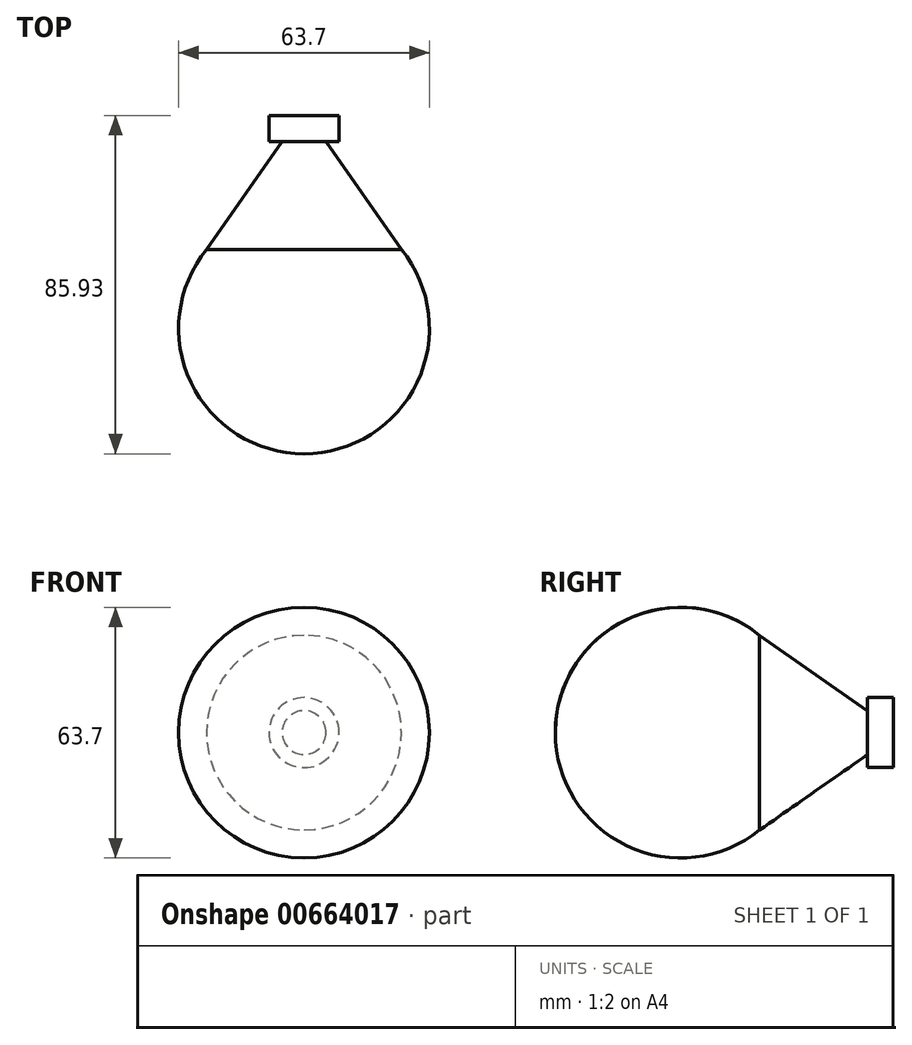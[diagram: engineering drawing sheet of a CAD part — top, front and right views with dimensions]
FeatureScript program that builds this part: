
annotation { "Feature Type Name" : "Feature", "Feature Type Description" : "" }
export const myFeature = defineFeature(function(context is Context, id is Id, definition is map)
    precondition{}
    {
        {
            var Q0;
            Q0=qCreatedBy(makeId("Front.planeOp"),FACE);
            var sketch = newSketch(context, id + "F0", { "sketchPlane" : qUnion([Q0])});
            skCircle(sketch, "E0", {"center": v(0, 0) * mm, "radius": 8.9 * mm});
            skSolve(sketch);
        }
        {
            var Q0;
            Q0=makeQuery(id+"F0.imprint","IMPRINT",FACE,{"disambiguationData":[TD([[makeQuery(id+"F0.imprint","IMPRINT",EDGE,{"derivedFrom":sQuery(id+"F0.wireOp",EDGE,"E0")}),1.0]])]});
            extrude(context, id + "F1", {"entities" : qUnion([Q0]), "oppositeDirection" : true, "depth" : 6.6 * mm, "offsetDistance" : 25.4 * mm});
        }
        {
            var Q0;
            Q0=qCreatedBy(makeId("Right.planeOp"),FACE);
            var sketch = newSketch(context, id + "F2", { "sketchPlane" : qUnion([Q0])});
            skCircle(sketch, "E1", {"center": v(-47.48, 0) * mm, "radius": 31.85 * mm});
            skPoint(sketch, "E2", {"position": v(0, 5.57) * mm});
            skLineSegment(sketch, "E3", {"start": v(-91.62, 0) * mm, "end": v(47.93, 0) * mm});
            skPoint(sketch, "E4.MirrorP", {"position": v(0, -5.57) * mm});
            skLineSegment(sketch, "E5", {"start": v(0, 5.57) * mm, "end": v(-27.42, 24.74) * mm});
            skLineSegment(sketch, "E6.MirrorCS", {"start": v(0, -5.57) * mm, "end": v(-27.42, -24.74) * mm});
            skLineSegment(sketch, "E7", {"start": v(0, 5.57) * mm, "end": v(0, -5.57) * mm});
            skSolve(sketch);
        }
        {
            var Q0;
            {var subQ0=sQuery(id+"F2.wireOp",EDGE,"E1");var subQ1=makeQuery(id+"F2.imprint","INTERSECT",VERTEX,{"derivedFrom":[subQ0,sQuery(id+"F2.wireOp",EDGE,"E5")]});Q0=makeQuery(id+"F2.imprint","IMPRINT",FACE,{"disambiguationData":[TD([[makeQuery(id+"F2.imprint","IMPRINT",EDGE,{"disambiguationData":[TD([[subQ1,1.0]])],"derivedFrom":subQ0}),1.0]])]});}
            var Q1;
            {var subQ0=sQuery(id+"F2.wireOp",EDGE,"E5");Q1=makeQuery(id+"F2.imprint","IMPRINT",FACE,{"disambiguationData":[TD([[makeQuery(id+"F2.imprint","IMPRINT",EDGE,{"derivedFrom":subQ0}),1.0]])]});}
            var Q2;
            Q2=sQuery(id+"F2.wireOp",EDGE,"E3");
            revolve(context, id + "F3", {"operationType" : NewBodyOperationType.ADD, "entities" : qUnion([Q0, Q1]), "axis" : qUnion([Q2]), "revolveType" : RevolveType.FULL});
        }
    });
